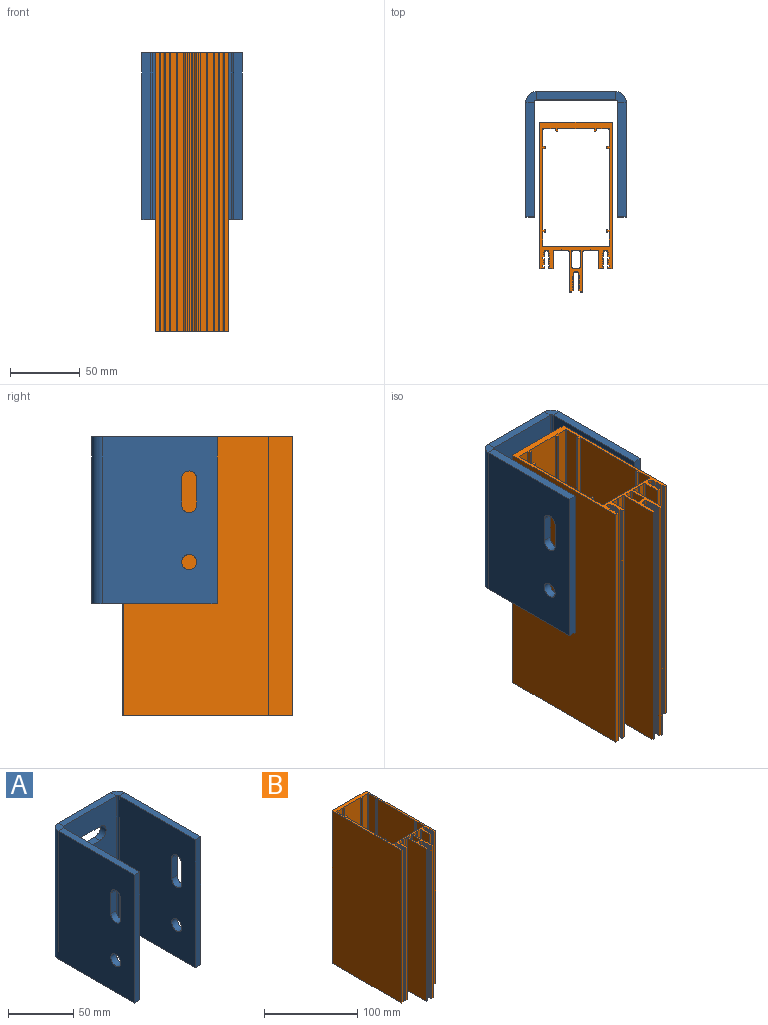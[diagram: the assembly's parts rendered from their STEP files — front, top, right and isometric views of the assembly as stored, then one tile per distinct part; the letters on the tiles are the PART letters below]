
ASSEMBLY  parts=2 mates=1
PART A: 41 faces, bbox 72x90x120 mm
  f0: plane 22x6mm, normal (0,0,-1), area 132mm2, adj f1,f10,f11,f12
  f1: cylinder r=6.5mm len=13mm, axis (0,1,0), area 122.5mm2, adj f0,f2,f11,f12
  f2: plane 22x6mm, normal (0,0,1), area 132mm2, adj f1,f10,f11,f12
  f3: plane 22x6mm, normal (0,0,-1), area 132mm2, adj f4,f9,f11,f12
  f4: cylinder r=6.5mm len=13mm, axis (0,1,0), area 122.5mm2, adj f3,f5,f11,f12
  f5: plane 22x6mm, normal (0,0,1), area 132mm2, adj f4,f9,f11,f12
  f6: plane 57x6mm, normal (0,0,1), area 342mm2, adj f11,f12,f24,f38
  f7: plane 57x6mm, normal (0,0,-1), area 342mm2, adj f11,f12,f23,f37
  f8: cylinder r=3mm len=6mm, axis (0,1,0), area 113.1mm2, adj f11,f12
  f9: cylinder r=6.5mm len=13mm, axis (0,1,0), area 122.5mm2, adj f3,f5,f11,f12
  f10: cylinder r=6.5mm len=13mm, axis (0,1,0), area 122.5mm2, adj f0,f2,f11,f12
  f11: plane 120x57mm, normal (0,1,0), area 5974.3mm2, adj f0,f1,f2,f3,f4,f5,f6,f7
  f12: plane 120x57mm, normal (0,-1,0), area 5974.3mm2, adj f0,f1,f2,f3,f4,f5,f6,f7
  f13: plane 82.5x6mm, normal (0,0,1), area 495mm2, adj f20,f21,f22,f24
  f14: plane 82.5x6mm, normal (0,0,-1), area 495mm2, adj f20,f21,f22,f23
  f15: plane 19x6mm, normal (0,1,0), area 114mm2, adj f16,f19,f21,f22
  f16: cylinder r=5.5mm len=11mm, axis (1,0,0), area 103.7mm2, adj f15,f17,f21,f22
  f17: plane 19x6mm, normal (0,-1,0), area 114mm2, adj f16,f19,f21,f22
  f18: cylinder r=5.5mm len=11mm, axis (1,0,0), area 207.3mm2, adj f21,f22
  f19: cylinder r=5.5mm len=11mm, axis (1,0,0), area 103.7mm2, adj f15,f17,f21,f22
  f20: plane 120x6mm, normal (0,-1,0), area 720mm2, adj f13,f14,f21,f22
  f21: plane 120x82.5mm, normal (-1,0,0), area 9500.9mm2, adj f13,f14,f15,f16,f17,f18,f19,f20
  f22: plane 120x82.5mm, normal (1,0,0), area 9500.9mm2, adj f13,f14,f15,f16,f17,f18,f19,f20
  f23: plane 7.5x7.5mm, normal (0,0,-1), area 42.4mm2, adj f7,f14,f25,f26
  f24: plane 7.5x7.5mm, normal (0,0,1), area 42.4mm2, adj f6,f13,f25,f26
  f25: cylinder r=7.5mm len=120mm, axis (0,0,-1), area 1413.7mm2, adj f11,f21,f23,f24
  f26: cylinder r=1.5mm len=120mm, axis (0,0,-1), area 282.7mm2, adj f12,f22,f23,f24
  f27: plane 19x6mm, normal (0,-1,0), area 114mm2, adj f28,f34,f35,f36
  f28: cylinder r=5.5mm len=11mm, axis (1,0,0), area 103.7mm2, adj f27,f29,f35,f36
  f29: plane 19x6mm, normal (0,1,0), area 114mm2, adj f28,f34,f35,f36
  f30: plane 82.5x6mm, normal (0,0,1), area 495mm2, adj f31,f35,f36,f38
  f31: plane 120x6mm, normal (0,-1,0), area 720mm2, adj f30,f32,f35,f36
  f32: plane 82.5x6mm, normal (0,0,-1), area 495mm2, adj f31,f35,f36,f37
  f33: cylinder r=5.5mm len=11mm, axis (1,0,0), area 207.3mm2, adj f35,f36
  f34: cylinder r=5.5mm len=11mm, axis (1,0,0), area 103.7mm2, adj f27,f29,f35,f36
  f35: plane 120x82.5mm, normal (1,0,0), area 9500.9mm2, adj f27,f28,f29,f30,f31,f32,f33,f34
  f36: plane 120x82.5mm, normal (-1,0,0), area 9500.9mm2, adj f27,f28,f29,f30,f31,f32,f33,f34
  f37: plane 7.5x7.5mm, normal (0,0,-1), area 42.4mm2, adj f7,f32,f39,f40
  f38: plane 7.5x7.5mm, normal (0,0,1), area 42.4mm2, adj f6,f30,f39,f40
  f39: cylinder r=7.5mm len=120mm, axis (0,0,-1), area 1413.7mm2, adj f11,f35,f37,f38
  f40: cylinder r=1.5mm len=120mm, axis (0,0,-1), area 282.7mm2, adj f12,f36,f37,f38
PART B: 291 faces, bbox 52x122x200 mm
  f0: cylinder r=1mm len=200mm, axis (0,0,-1), area 314.2mm2, adj f1,f288,f289,f290
  f1: plane 200x4mm, normal (0,-1,0), area 800mm2, adj f0,f2,f289,f290
  f2: cylinder r=1mm len=200mm, axis (0,0,-1), area 314.2mm2, adj f1,f3,f289,f290
  f3: plane 200x11mm, normal (-1,0,0), area 2200mm2, adj f2,f4,f289,f290
  f4: cylinder r=1mm len=200mm, axis (0,0,-1), area 314.2mm2, adj f3,f5,f289,f290
  f5: plane 200x4mm, normal (0,1,0), area 800mm2, adj f4,f6,f289,f290
  f6: cylinder r=1mm len=200mm, axis (0,0,-1), area 314.2mm2, adj f5,f288,f289,f290
  f7: plane 200x12.4mm, normal (-1,0,0), area 2480mm2, adj f8,f286,f289,f290
  f8: plane 200x2.15mm, normal (0,1,0), area 430mm2, adj f7,f9,f289,f290
  f9: plane 200x1.5mm, normal (-1,0,0), area 300mm2, adj f8,f10,f289,f290
  f10: plane 200x2.15mm, normal (0,-1,0), area 430mm2, adj f9,f11,f289,f290
  f11: plane 200x58.3mm, normal (-1,0,0), area 11660mm2, adj f10,f12,f289,f290
  f12: plane 200x2.15mm, normal (0,1,0), area 430mm2, adj f11,f13,f289,f290
  f13: plane 200x1.5mm, normal (-1,0,0), area 300mm2, adj f12,f14,f289,f290
  f14: plane 200x2.15mm, normal (0,-1,0), area 430mm2, adj f13,f15,f289,f290
  f15: plane 200x10.5mm, normal (-1,0,0), area 2100mm2, adj f14,f16,f289,f290
  f16: cylinder r=0.5mm len=200mm, axis (0,0,-1), area 157.1mm2, adj f15,f17,f289,f290
  f17: plane 200x46.8mm, normal (0,1,0), area 9360mm2, adj f16,f18,f289,f290
  f18: cylinder r=0.5mm len=200mm, axis (0,0,-1), area 157.1mm2, adj f17,f19,f289,f290
  f19: plane 200x10.5mm, normal (1,0,0), area 2100mm2, adj f18,f20,f289,f290
  f20: plane 200x2.15mm, normal (0,-1,0), area 430mm2, adj f19,f21,f289,f290
  f21: plane 200x1.5mm, normal (1,0,0), area 300mm2, adj f20,f22,f289,f290
  f22: plane 200x2.15mm, normal (0,1,0), area 430mm2, adj f21,f23,f289,f290
  f23: plane 200x58.3mm, normal (1,0,0), area 11660mm2, adj f22,f24,f289,f290
  f24: plane 200x2.15mm, normal (0,-1,0), area 430mm2, adj f23,f25,f289,f290
  f25: plane 200x1.5mm, normal (1,0,0), area 300mm2, adj f24,f26,f289,f290
  f26: plane 200x2.15mm, normal (0,1,0), area 430mm2, adj f25,f27,f289,f290
  f27: plane 200x12.4mm, normal (1,0,0), area 2480mm2, adj f26,f28,f289,f290
  f28: cylinder r=0.5mm len=200mm, axis (0,0,-1), area 157.1mm2, adj f27,f29,f289,f290
  f29: plane 200x8.6mm, normal (0,-1,0), area 1720mm2, adj f28,f30,f289,f290
  f30: plane 200x1.9mm, normal (-0.94,-0.35,0), area 405mm2, adj f29,f31,f289,f290
  f31: plane 200x1.1mm, normal (0,-1,0), area 220mm2, adj f30,f32,f289,f290
  f32: plane 200x1.9mm, normal (1,0,0), area 380mm2, adj f31,f33,f289,f290
  f33: plane 200x26mm, normal (0,-1,0), area 5200mm2, adj f32,f34,f289,f290
  f34: plane 200x1.9mm, normal (-1,0,0), area 380mm2, adj f33,f35,f289,f290
  f35: plane 200x1.1mm, normal (0,-1,0), area 220mm2, adj f34,f36,f289,f290
  f36: plane 200x1.9mm, normal (0.94,-0.35,0), area 405mm2, adj f35,f37,f289,f290
  f37: plane 200x8.6mm, normal (0,-1,0), area 1720mm2, adj f36,f286,f289,f290
  f38: plane 200x1.7mm, normal (0,-1,0), area 340mm2, adj f39,f287,f289,f290
  f39: plane 200x29mm, normal (1,0,0), area 5800mm2, adj f38,f40,f289,f290
  f40: cylinder r=1mm len=200mm, axis (0,0,-1), area 314.2mm2, adj f39,f41,f289,f290
  f41: plane 200x4.45mm, normal (0,-1,0), area 890mm2, adj f40,f42,f289,f290
  f42: plane 200x0.3mm, normal (0.71,-0.71,0), area 84.9mm2, adj f41,f43,f289,f290
  f43: plane 200x0.3mm, normal (-0.71,-0.71,0), area 84.9mm2, adj f42,f44,f289,f290
  f44: plane 200x4.45mm, normal (0,-1,0), area 890mm2, adj f43,f45,f289,f290
  f45: cylinder r=1mm len=200mm, axis (0,0,-1), area 314.2mm2, adj f44,f46,f289,f290
  f46: plane 200x12mm, normal (-1,0,0), area 2400mm2, adj f45,f47,f289,f290
  f47: plane 200x2.69mm, normal (0,-1,0), area 538mm2, adj f46,f48,f289,f290
  f48: plane 200x0.5mm, normal (0.71,-0.71,0), area 141.4mm2, adj f47,f49,f289,f290
  f49: plane 200x0.5mm, normal (1,0,0), area 100mm2, adj f48,f50,f289,f290
  f50: plane 200x1mm, normal (0,1,0), area 200mm2, adj f49,f51,f289,f290
  f51: plane 200x0.93mm, normal (1,0,0), area 186.6mm2, adj f50,f52,f289,f290
  f52: plane 200x1mm, normal (0.71,-0.71,0), area 282.3mm2, adj f51,f53,f289,f290
  f53: cylinder r=0.3mm len=200mm, axis (0,0,-1), area 64.9mm2, adj f52,f54,f289,f290
  f54: plane 200x0.15mm, normal (0.5,0.87,0), area 34.6mm2, adj f53,f55,f289,f290
  f55: cylinder r=0.2mm len=200mm, axis (0,0,-1), area 83.8mm2, adj f54,f56,f289,f290
  f56: plane 200x0.15mm, normal (0.5,-0.87,0), area 34.6mm2, adj f55,f57,f289,f290
  f57: cylinder r=0.3mm len=200mm, axis (0,0,-1), area 62.8mm2, adj f56,f58,f289,f290
  f58: plane 200x0.36mm, normal (1,0,0), area 72.2mm2, adj f57,f59,f289,f290
  f59: cylinder r=0.3mm len=200mm, axis (0,0,-1), area 62.8mm2, adj f58,f60,f289,f290
  f60: plane 200x0.15mm, normal (0.5,0.87,0), area 34.6mm2, adj f59,f61,f289,f290
  f61: cylinder r=0.2mm len=200mm, axis (0,0,-1), area 83.8mm2, adj f60,f62,f289,f290
  f62: plane 200x0.15mm, normal (0.5,-0.87,0), area 34.6mm2, adj f61,f63,f289,f290
  f63: cylinder r=0.3mm len=200mm, axis (0,0,-1), area 62.8mm2, adj f62,f64,f289,f290
  f64: plane 200x0.36mm, normal (1,0,0), area 72.2mm2, adj f63,f65,f289,f290
  f65: cylinder r=0.3mm len=200mm, axis (0,0,-1), area 62.8mm2, adj f64,f66,f289,f290
  f66: plane 200x0.15mm, normal (0.5,0.87,0), area 34.6mm2, adj f65,f67,f289,f290
  f67: cylinder r=0.2mm len=200mm, axis (0,0,-1), area 83.8mm2, adj f66,f68,f289,f290
  f68: plane 200x0.15mm, normal (0.5,-0.87,0), area 34.6mm2, adj f67,f69,f289,f290
  f69: cylinder r=0.3mm len=200mm, axis (0,0,-1), area 62.8mm2, adj f68,f70,f289,f290
  f70: plane 200x0.22mm, normal (1,0,0), area 44.2mm2, adj f69,f71,f289,f290
  f71: plane 200x1mm, normal (0,1,0), area 200mm2, adj f70,f72,f289,f290
  f72: plane 200x0.93mm, normal (1,0,0), area 186.6mm2, adj f71,f73,f289,f290
  f73: plane 200x0.86mm, normal (0.71,-0.71,0), area 243.4mm2, adj f72,f74,f289,f290
  f74: cylinder r=0.3mm len=200mm, axis (0,0,-1), area 2.8mm2, adj f73,f75,f289,f290
  f75: plane 200x0.15mm, normal (0.5,0.87,0), area 34.6mm2, adj f74,f76,f289,f290
  f76: cylinder r=0.2mm len=200mm, axis (0,0,-1), area 83.8mm2, adj f75,f77,f289,f290
  f77: plane 200x0.15mm, normal (0.5,-0.87,0), area 34.6mm2, adj f76,f78,f289,f290
  f78: cylinder r=0.3mm len=200mm, axis (0,0,-1), area 62.8mm2, adj f77,f79,f289,f290
  f79: plane 200x0.36mm, normal (1,0,0), area 72.2mm2, adj f78,f80,f289,f290
  f80: cylinder r=0.3mm len=200mm, axis (0,0,-1), area 62.8mm2, adj f79,f81,f289,f290
  f81: plane 200x0.15mm, normal (0.5,0.87,0), area 34.6mm2, adj f80,f82,f289,f290
  f82: cylinder r=0.2mm len=200mm, axis (0,0,-1), area 83.8mm2, adj f81,f83,f289,f290
  f83: plane 200x0.15mm, normal (0.5,-0.87,0), area 34.6mm2, adj f82,f84,f289,f290
  f84: cylinder r=0.3mm len=200mm, axis (0,0,-1), area 62.8mm2, adj f83,f85,f289,f290
  f85: plane 200x0.46mm, normal (1,0,0), area 92.2mm2, adj f84,f86,f289,f290
  f86: cylinder r=1.56mm len=200mm, axis (0,0,-1), area 938.3mm2, adj f85,f87,f289,f290
  f87: cylinder r=0.3mm len=200mm, axis (0,0,-1), area 54.8mm2, adj f86,f88,f289,f290
  f88: plane 200x0.17mm, normal (-0.5,-0.87,0), area 38.5mm2, adj f87,f89,f289,f290
  f89: cylinder r=0.2mm len=200mm, axis (0,0,-1), area 83.8mm2, adj f88,f90,f289,f290
  f90: plane 200x0.15mm, normal (-0.5,0.87,0), area 34.6mm2, adj f89,f91,f289,f290
  f91: cylinder r=0.3mm len=200mm, axis (0,0,-1), area 62.8mm2, adj f90,f92,f289,f290
  f92: plane 200x0.36mm, normal (-1,0,0), area 72.2mm2, adj f91,f93,f289,f290
  f93: cylinder r=0.3mm len=200mm, axis (0,0,-1), area 62.8mm2, adj f92,f94,f289,f290
  f94: plane 200x0.15mm, normal (-0.5,-0.87,0), area 34.6mm2, adj f93,f95,f289,f290
  f95: cylinder r=0.2mm len=200mm, axis (0,0,-1), area 83.8mm2, adj f94,f96,f289,f290
  f96: plane 200x0.15mm, normal (-0.5,0.87,0), area 34.6mm2, adj f95,f97,f289,f290
  f97: cylinder r=0.3mm len=200mm, axis (0,0,-1), area 62.8mm2, adj f96,f98,f289,f290
  f98: plane 200x0.31mm, normal (-1,0,0), area 62mm2, adj f97,f99,f289,f290
  f99: plane 200x1mm, normal (-0.71,-0.71,0), area 282.4mm2, adj f98,f100,f289,f290
  f100: plane 200x0.93mm, normal (-1,0,0), area 186.6mm2, adj f99,f101,f289,f290
  f101: plane 200x1mm, normal (0,1,0), area 200mm2, adj f100,f102,f289,f290
  f102: plane 200x0.92mm, normal (-1,0,0), area 184.2mm2, adj f101,f103,f289,f290
  f103: cylinder r=0.3mm len=200mm, axis (0,0,-1), area 62.8mm2, adj f102,f104,f289,f290
  f104: plane 200x0.15mm, normal (-0.5,-0.87,0), area 34.6mm2, adj f103,f105,f289,f290
  f105: cylinder r=0.2mm len=200mm, axis (0,0,-1), area 83.8mm2, adj f104,f106,f289,f290
  f106: plane 200x0.15mm, normal (-0.5,0.87,0), area 34.6mm2, adj f105,f107,f289,f290
  f107: cylinder r=0.3mm len=200mm, axis (0,0,-1), area 62.8mm2, adj f106,f108,f289,f290
  f108: plane 200x0.36mm, normal (-1,0,0), area 72.2mm2, adj f107,f109,f289,f290
  f109: cylinder r=0.3mm len=200mm, axis (0,0,-1), area 62.8mm2, adj f108,f110,f289,f290
  f110: plane 200x0.15mm, normal (-0.5,-0.87,0), area 34.6mm2, adj f109,f111,f289,f290
  f111: cylinder r=0.2mm len=200mm, axis (0,0,-1), area 83.8mm2, adj f110,f112,f289,f290
  f112: plane 200x0.15mm, normal (-0.5,0.87,0), area 34.6mm2, adj f111,f113,f289,f290
  f113: cylinder r=0.3mm len=200mm, axis (0,0,-1), area 62.8mm2, adj f112,f114,f289,f290
  f114: plane 200x0.71mm, normal (-1,0,0), area 142mm2, adj f113,f115,f289,f290
  f115: plane 200x1mm, normal (-0.71,-0.71,0), area 282.4mm2, adj f114,f116,f289,f290
  f116: plane 200x0.93mm, normal (-1,0,0), area 186.6mm2, adj f115,f117,f289,f290
  f117: plane 200x1mm, normal (0,1,0), area 200mm2, adj f116,f118,f289,f290
  f118: plane 200x0.5mm, normal (-1,0,0), area 100mm2, adj f117,f119,f289,f290
  f119: plane 200x0.5mm, normal (-0.71,-0.71,0), area 141.4mm2, adj f118,f120,f289,f290
  f120: plane 200x2.69mm, normal (0,-1,0), area 538mm2, adj f119,f121,f289,f290
  f121: plane 200x104.5mm, normal (1,0,0), area 20900mm2, adj f120,f122,f289,f290
  f122: cylinder r=0.5mm len=200mm, axis (0,0,-1), area 157.1mm2, adj f121,f123,f289,f290
  f123: plane 200x51mm, normal (0,1,0), area 10200mm2, adj f122,f124,f289,f290
  f124: cylinder r=0.5mm len=200mm, axis (0,0,-1), area 157.1mm2, adj f123,f125,f289,f290
  f125: plane 200x104.5mm, normal (-1,0,0), area 20900mm2, adj f124,f126,f289,f290
  f126: plane 200x2.69mm, normal (0,-1,0), area 538mm2, adj f125,f127,f289,f290
  f127: plane 200x0.5mm, normal (0.71,-0.71,0), area 141.4mm2, adj f126,f128,f289,f290
  f128: plane 200x0.5mm, normal (1,0,0), area 100mm2, adj f127,f129,f289,f290
  f129: plane 200x1mm, normal (0,1,0), area 200mm2, adj f128,f130,f289,f290
  f130: plane 200x0.93mm, normal (1,0,0), area 186.6mm2, adj f129,f131,f289,f290
  f131: plane 200x1mm, normal (0.71,-0.71,0), area 282.4mm2, adj f130,f132,f289,f290
  f132: plane 200x0.71mm, normal (1,0,0), area 142mm2, adj f131,f133,f289,f290
  f133: cylinder r=0.3mm len=200mm, axis (0,0,-1), area 62.8mm2, adj f132,f134,f289,f290
  f134: plane 200x0.15mm, normal (0.5,0.87,0), area 34.6mm2, adj f133,f135,f289,f290
  f135: cylinder r=0.2mm len=200mm, axis (0,0,-1), area 83.8mm2, adj f134,f136,f289,f290
  f136: plane 200x0.15mm, normal (0.5,-0.87,0), area 34.6mm2, adj f135,f137,f289,f290
  f137: cylinder r=0.3mm len=200mm, axis (0,0,-1), area 62.8mm2, adj f136,f138,f289,f290
  f138: plane 200x0.36mm, normal (1,0,0), area 72.2mm2, adj f137,f139,f289,f290
  f139: cylinder r=0.3mm len=200mm, axis (0,0,-1), area 62.8mm2, adj f138,f140,f289,f290
  f140: plane 200x0.15mm, normal (0.5,0.87,0), area 34.6mm2, adj f139,f141,f289,f290
  f141: cylinder r=0.2mm len=200mm, axis (0,0,-1), area 83.8mm2, adj f140,f142,f289,f290
  f142: plane 200x0.15mm, normal (0.5,-0.87,0), area 34.6mm2, adj f141,f143,f289,f290
  f143: cylinder r=0.3mm len=200mm, axis (0,0,-1), area 62.8mm2, adj f142,f144,f289,f290
  f144: plane 200x0.92mm, normal (1,0,0), area 184.2mm2, adj f143,f145,f289,f290
  f145: plane 200x1mm, normal (0,1,0), area 200mm2, adj f144,f146,f289,f290
  f146: plane 200x0.93mm, normal (1,0,0), area 186.6mm2, adj f145,f147,f289,f290
  f147: plane 200x1mm, normal (0.71,-0.71,0), area 282.4mm2, adj f146,f148,f289,f290
  f148: plane 200x0.31mm, normal (1,0,0), area 62mm2, adj f147,f149,f289,f290
  f149: cylinder r=0.3mm len=200mm, axis (0,0,-1), area 62.8mm2, adj f148,f150,f289,f290
  f150: plane 200x0.15mm, normal (0.5,0.87,0), area 34.6mm2, adj f149,f151,f289,f290
  f151: cylinder r=0.2mm len=200mm, axis (0,0,-1), area 83.8mm2, adj f150,f152,f289,f290
  f152: plane 200x0.15mm, normal (0.5,-0.87,0), area 34.6mm2, adj f151,f153,f289,f290
  f153: cylinder r=0.3mm len=200mm, axis (0,0,-1), area 62.8mm2, adj f152,f154,f289,f290
  f154: plane 200x0.36mm, normal (1,0,0), area 72.2mm2, adj f153,f155,f289,f290
  f155: cylinder r=0.3mm len=200mm, axis (0,0,-1), area 62.8mm2, adj f154,f156,f289,f290
  f156: plane 200x0.15mm, normal (0.5,0.87,0), area 34.6mm2, adj f155,f157,f289,f290
  f157: cylinder r=0.2mm len=200mm, axis (0,0,-1), area 83.8mm2, adj f156,f158,f289,f290
  f158: plane 200x0.17mm, normal (0.5,-0.87,0), area 38.5mm2, adj f157,f159,f289,f290
  f159: cylinder r=0.3mm len=200mm, axis (0,0,-1), area 54.8mm2, adj f158,f160,f289,f290
  f160: cylinder r=1.56mm len=200mm, axis (0,0,-1), area 938.3mm2, adj f159,f161,f289,f290
  f161: plane 200x0.46mm, normal (-1,0,0), area 92.2mm2, adj f160,f162,f289,f290
  f162: cylinder r=0.3mm len=200mm, axis (0,0,-1), area 62.8mm2, adj f161,f163,f289,f290
  f163: plane 200x0.15mm, normal (-0.5,-0.87,0), area 34.6mm2, adj f162,f164,f289,f290
  f164: cylinder r=0.2mm len=200mm, axis (0,0,-1), area 83.8mm2, adj f163,f165,f289,f290
  f165: plane 200x0.15mm, normal (-0.5,0.87,0), area 34.6mm2, adj f164,f166,f289,f290
  f166: cylinder r=0.3mm len=200mm, axis (0,0,-1), area 62.8mm2, adj f165,f167,f289,f290
  f167: plane 200x0.36mm, normal (-1,0,0), area 72.2mm2, adj f166,f168,f289,f290
  f168: cylinder r=0.3mm len=200mm, axis (0,0,-1), area 62.8mm2, adj f167,f169,f289,f290
  f169: plane 200x0.15mm, normal (-0.5,-0.87,0), area 34.6mm2, adj f168,f170,f289,f290
  f170: cylinder r=0.2mm len=200mm, axis (0,0,-1), area 83.8mm2, adj f169,f171,f289,f290
  f171: plane 200x0.15mm, normal (-0.5,0.87,0), area 34.6mm2, adj f170,f172,f289,f290
  f172: cylinder r=0.3mm len=200mm, axis (0,0,-1), area 2.8mm2, adj f171,f173,f289,f290
  f173: plane 200x0.86mm, normal (-0.71,-0.71,0), area 243.4mm2, adj f172,f174,f289,f290
  f174: plane 200x0.93mm, normal (-1,0,0), area 186.6mm2, adj f173,f175,f289,f290
  f175: plane 200x1mm, normal (0,1,0), area 200mm2, adj f174,f176,f289,f290
  f176: plane 200x0.22mm, normal (-1,0,0), area 44.2mm2, adj f175,f177,f289,f290
  f177: cylinder r=0.3mm len=200mm, axis (0,0,-1), area 62.8mm2, adj f176,f178,f289,f290
  f178: plane 200x0.15mm, normal (-0.5,-0.87,0), area 34.6mm2, adj f177,f179,f289,f290
  f179: cylinder r=0.2mm len=200mm, axis (0,0,-1), area 83.8mm2, adj f178,f180,f289,f290
  f180: plane 200x0.15mm, normal (-0.5,0.87,0), area 34.6mm2, adj f179,f181,f289,f290
  f181: cylinder r=0.3mm len=200mm, axis (0,0,-1), area 62.8mm2, adj f180,f182,f289,f290
  f182: plane 200x0.36mm, normal (-1,0,0), area 72.2mm2, adj f181,f183,f289,f290
  f183: cylinder r=0.3mm len=200mm, axis (0,0,-1), area 62.8mm2, adj f182,f184,f289,f290
  f184: plane 200x0.15mm, normal (-0.5,-0.87,0), area 34.6mm2, adj f183,f185,f289,f290
  f185: cylinder r=0.2mm len=200mm, axis (0,0,-1), area 83.8mm2, adj f184,f186,f289,f290
  f186: plane 200x0.15mm, normal (-0.5,0.87,0), area 34.6mm2, adj f185,f187,f289,f290
  f187: cylinder r=0.3mm len=200mm, axis (0,0,-1), area 62.8mm2, adj f186,f188,f289,f290
  f188: plane 200x0.36mm, normal (-1,0,0), area 72.2mm2, adj f187,f189,f289,f290
  f189: cylinder r=0.3mm len=200mm, axis (0,0,-1), area 62.8mm2, adj f188,f190,f289,f290
  f190: plane 200x0.15mm, normal (-0.5,-0.87,0), area 34.6mm2, adj f189,f191,f289,f290
  f191: cylinder r=0.2mm len=200mm, axis (0,0,-1), area 83.8mm2, adj f190,f192,f289,f290
  f192: plane 200x0.15mm, normal (-0.5,0.87,0), area 34.6mm2, adj f191,f193,f289,f290
  f193: cylinder r=0.3mm len=200mm, axis (0,0,-1), area 64.9mm2, adj f192,f194,f289,f290
  f194: plane 200x1mm, normal (-0.71,-0.71,0), area 282.3mm2, adj f193,f195,f289,f290
  f195: plane 200x0.93mm, normal (-1,0,0), area 186.6mm2, adj f194,f196,f289,f290
  f196: plane 200x1mm, normal (0,1,0), area 200mm2, adj f195,f197,f289,f290
  f197: plane 200x0.5mm, normal (-1,0,0), area 100mm2, adj f196,f198,f289,f290
  f198: plane 200x0.5mm, normal (-0.71,-0.71,0), area 141.4mm2, adj f197,f199,f289,f290
  f199: plane 200x2.69mm, normal (0,-1,0), area 538mm2, adj f198,f200,f289,f290
  f200: plane 200x12mm, normal (1,0,0), area 2400mm2, adj f199,f201,f289,f290
  f201: cylinder r=1mm len=200mm, axis (0,0,-1), area 314.2mm2, adj f200,f202,f289,f290
  f202: plane 200x4.45mm, normal (0,-1,0), area 890mm2, adj f201,f203,f289,f290
  f203: plane 200x0.3mm, normal (0.71,-0.71,0), area 84.9mm2, adj f202,f204,f289,f290
  f204: plane 200x0.3mm, normal (-0.71,-0.71,0), area 84.9mm2, adj f203,f205,f289,f290
  f205: plane 200x4.45mm, normal (0,-1,0), area 890mm2, adj f204,f206,f289,f290
  f206: cylinder r=1mm len=200mm, axis (0,0,-1), area 314.2mm2, adj f205,f207,f289,f290
  f207: plane 200x29mm, normal (-1,0,0), area 5800mm2, adj f206,f208,f289,f290
  f208: plane 200x1.7mm, normal (0,-1,0), area 340mm2, adj f207,f209,f289,f290
  f209: plane 200x1.2mm, normal (0.71,-0.71,0), area 339mm2, adj f208,f210,f289,f290
  f210: cylinder r=0.18mm len=200mm, axis (0,0,-1), area 64.6mm2, adj f209,f211,f289,f290
  f211: plane 200x0.26mm, normal (0.5,0.87,0), area 60.5mm2, adj f210,f212,f289,f290
  f212: cylinder r=0.2mm len=200mm, axis (0,0,-1), area 83.8mm2, adj f211,f213,f289,f290
  f213: plane 200x0.2mm, normal (0.5,-0.87,0), area 46.2mm2, adj f212,f214,f289,f290
  f214: cylinder r=0.3mm len=200mm, axis (0,0,-1), area 62.8mm2, adj f213,f215,f289,f290
  f215: plane 200x0.7mm, normal (1,0,0), area 140.6mm2, adj f214,f216,f289,f290
  f216: cylinder r=0.3mm len=200mm, axis (0,0,-1), area 62.8mm2, adj f215,f217,f289,f290
  f217: plane 200x0.2mm, normal (0.5,0.87,0), area 46.2mm2, adj f216,f218,f289,f290
  f218: cylinder r=0.2mm len=200mm, axis (0,0,-1), area 83.8mm2, adj f217,f219,f289,f290
  f219: plane 200x0.2mm, normal (0.5,-0.87,0), area 46.2mm2, adj f218,f220,f289,f290
  f220: cylinder r=0.3mm len=200mm, axis (0,0,-1), area 62.8mm2, adj f219,f221,f289,f290
  f221: plane 200x0.7mm, normal (1,0,0), area 140.6mm2, adj f220,f222,f289,f290
  f222: cylinder r=0.3mm len=200mm, axis (0,0,-1), area 62.8mm2, adj f221,f223,f289,f290
  f223: plane 200x0.2mm, normal (0.5,0.87,0), area 46.2mm2, adj f222,f224,f289,f290
  f224: cylinder r=0.2mm len=200mm, axis (0,0,-1), area 83.8mm2, adj f223,f225,f289,f290
  f225: plane 200x0.2mm, normal (0.5,-0.87,0), area 46.2mm2, adj f224,f226,f289,f290
  f226: cylinder r=0.3mm len=200mm, axis (0,0,-1), area 62.8mm2, adj f225,f227,f289,f290
  f227: plane 200x0.7mm, normal (1,0,0), area 140.6mm2, adj f226,f228,f289,f290
  f228: cylinder r=0.3mm len=200mm, axis (0,0,-1), area 62.8mm2, adj f227,f229,f289,f290
  f229: plane 200x0.2mm, normal (0.5,0.87,0), area 46.2mm2, adj f228,f230,f289,f290
  f230: cylinder r=0.2mm len=200mm, axis (0,0,-1), area 83.8mm2, adj f229,f231,f289,f290
  f231: plane 200x0.2mm, normal (0.5,-0.87,0), area 46.2mm2, adj f230,f232,f289,f290
  f232: cylinder r=0.3mm len=200mm, axis (0,0,-1), area 62.8mm2, adj f231,f233,f289,f290
  f233: plane 200x0.7mm, normal (1,0,0), area 140.6mm2, adj f232,f234,f289,f290
  f234: cylinder r=0.3mm len=200mm, axis (0,0,-1), area 62.8mm2, adj f233,f235,f289,f290
  f235: plane 200x0.2mm, normal (0.5,0.87,0), area 46.2mm2, adj f234,f236,f289,f290
  f236: cylinder r=0.2mm len=200mm, axis (0,0,-1), area 83.8mm2, adj f235,f237,f289,f290
  f237: plane 200x0.2mm, normal (0.5,-0.87,0), area 46.2mm2, adj f236,f238,f289,f290
  f238: cylinder r=0.3mm len=200mm, axis (0,0,-1), area 62.8mm2, adj f237,f239,f289,f290
  f239: plane 200x0.7mm, normal (1,0,0), area 140.6mm2, adj f238,f240,f289,f290
  f240: cylinder r=0.3mm len=200mm, axis (0,0,-1), area 62.8mm2, adj f239,f241,f289,f290
  f241: plane 200x0.2mm, normal (0.5,0.87,0), area 46.2mm2, adj f240,f242,f289,f290
  f242: cylinder r=0.2mm len=200mm, axis (0,0,-1), area 83.8mm2, adj f241,f243,f289,f290
  f243: plane 200x0.15mm, normal (0.5,-0.87,0), area 34.6mm2, adj f242,f244,f289,f290
  f244: cylinder r=0.3mm len=200mm, axis (0,0,-1), area 62.8mm2, adj f243,f245,f289,f290
  f245: plane 200x1.58mm, normal (1,0,0), area 316.1mm2, adj f244,f246,f289,f290
  f246: cylinder r=1.5mm len=200mm, axis (0,0,-1), area 471.2mm2, adj f245,f247,f289,f290
  f247: plane 200x1.2mm, normal (0,-1,0), area 240mm2, adj f246,f248,f289,f290
  f248: cylinder r=1.5mm len=200mm, axis (0,0,-1), area 471.2mm2, adj f247,f249,f289,f290
  f249: plane 200x0.68mm, normal (-1,0,0), area 136.3mm2, adj f248,f250,f289,f290
  f250: cylinder r=0.3mm len=200mm, axis (0,0,-1), area 62.6mm2, adj f249,f251,f289,f290
  f251: plane 200x0.15mm, normal (-0.5,-0.87,0), area 34.6mm2, adj f250,f252,f289,f290
  f252: cylinder r=0.2mm len=200mm, axis (0,0,-1), area 83.8mm2, adj f251,f253,f289,f290
  f253: plane 200x0.2mm, normal (-0.5,0.87,0), area 46.2mm2, adj f252,f254,f289,f290
  f254: cylinder r=0.3mm len=200mm, axis (0,0,-1), area 62.8mm2, adj f253,f255,f289,f290
  f255: plane 200x0.7mm, normal (-1,0,0), area 140.6mm2, adj f254,f256,f289,f290
  f256: cylinder r=0.3mm len=200mm, axis (0,0,-1), area 62.8mm2, adj f255,f257,f289,f290
  f257: plane 200x0.2mm, normal (-0.5,-0.87,0), area 46.2mm2, adj f256,f258,f289,f290
  f258: cylinder r=0.2mm len=200mm, axis (0,0,-1), area 83.8mm2, adj f257,f259,f289,f290
  f259: plane 200x0.2mm, normal (-0.5,0.87,0), area 46.2mm2, adj f258,f260,f289,f290
  f260: cylinder r=0.3mm len=200mm, axis (0,0,-1), area 62.8mm2, adj f259,f261,f289,f290
  f261: plane 200x0.7mm, normal (-1,0,0), area 140.6mm2, adj f260,f262,f289,f290
  f262: cylinder r=0.3mm len=200mm, axis (0,0,-1), area 62.8mm2, adj f261,f263,f289,f290
  f263: plane 200x0.2mm, normal (-0.5,-0.87,0), area 46.2mm2, adj f262,f264,f289,f290
  f264: cylinder r=0.2mm len=200mm, axis (0,0,-1), area 83.8mm2, adj f263,f265,f289,f290
  f265: plane 200x0.2mm, normal (-0.5,0.87,0), area 46.2mm2, adj f264,f266,f289,f290
  f266: cylinder r=0.3mm len=200mm, axis (0,0,-1), area 62.8mm2, adj f265,f267,f289,f290
  f267: plane 200x0.7mm, normal (-1,0,0), area 140.6mm2, adj f266,f268,f289,f290
  f268: cylinder r=0.3mm len=200mm, axis (0,0,-1), area 62.8mm2, adj f267,f269,f289,f290
  f269: plane 200x0.2mm, normal (-0.5,-0.87,0), area 46.2mm2, adj f268,f270,f289,f290
  f270: cylinder r=0.2mm len=200mm, axis (0,0,-1), area 83.8mm2, adj f269,f271,f289,f290
  f271: plane 200x0.2mm, normal (-0.5,0.87,0), area 46.2mm2, adj f270,f272,f289,f290
  f272: cylinder r=0.3mm len=200mm, axis (0,0,-1), area 62.8mm2, adj f271,f273,f289,f290
  f273: plane 200x0.7mm, normal (-1,0,0), area 140.6mm2, adj f272,f274,f289,f290
  f274: cylinder r=0.3mm len=200mm, axis (0,0,-1), area 62.8mm2, adj f273,f275,f289,f290
  f275: plane 200x0.2mm, normal (-0.5,-0.87,0), area 46.2mm2, adj f274,f276,f289,f290
  f276: cylinder r=0.2mm len=200mm, axis (0,0,-1), area 83.8mm2, adj f275,f277,f289,f290
  f277: plane 200x0.2mm, normal (-0.5,0.87,0), area 46.4mm2, adj f276,f278,f289,f290
  f278: cylinder r=0.3mm len=200mm, axis (0,0,-1), area 62.8mm2, adj f277,f279,f289,f290
  f279: plane 200x0.7mm, normal (-1,0,0), area 140.4mm2, adj f278,f280,f289,f290
  f280: cylinder r=0.3mm len=200mm, axis (0,0,-1), area 62.8mm2, adj f279,f281,f289,f290
  f281: plane 200x0.2mm, normal (-0.5,-0.87,0), area 46.4mm2, adj f280,f282,f289,f290
  f282: cylinder r=0.2mm len=200mm, axis (0,0,-1), area 83.8mm2, adj f281,f283,f289,f290
  f283: plane 200x0.2mm, normal (-0.5,0.87,0), area 46.4mm2, adj f282,f284,f289,f290
  f284: cylinder r=0.3mm len=200mm, axis (0,0,-1), area 62.8mm2, adj f283,f285,f289,f290
  f285: plane 200x0.9mm, normal (-1,0,0), area 180mm2, adj f284,f287,f289,f290
  f286: cylinder r=0.5mm len=200mm, axis (0,0,-1), area 157.1mm2, adj f7,f37,f289,f290
  f287: plane 200x1.25mm, normal (-0.71,-0.71,0), area 353.8mm2, adj f38,f285,f289,f290
  f288: plane 200x11mm, normal (1,0,0), area 2200mm2, adj f0,f6,f289,f290
  f289: plane 122x52mm, normal (0,0,1), area 1043.5mm2, adj f0,f1,f2,f3,f4,f5,f6,f7
  f290: plane 122x52mm, normal (0,0,-1), area 1043.5mm2, adj f0,f1,f2,f3,f4,f5,f6,f7
PLACE A t=(-116.74,75.01,77.54)mm
PLACE B t=(-80.74,-7.99,-2.46)mm
MATE fastened A.f6 <-> B.f289  axis (0,0,1) through (-80.74,53.01,197.54)mm
